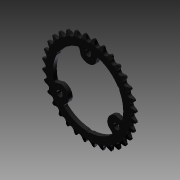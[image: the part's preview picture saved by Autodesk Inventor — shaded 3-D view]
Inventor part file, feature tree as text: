
AUTODESK INVENTOR PART (.ipt)
format: ipt  version: 2012 (Build 160160000, 160)  size: 849,408 bytes
history: native  units: in
note: dims shown in document units (in); Inventor stores cm internally (conversion verified against a paired STEP export)
features: boolean_combine x1, extrude x1, imported_body x1, sketch x1
ambient origin geometry x8: Origin, YZ Plane, XZ Plane, XY Plane, X Axis, Y Axis, Z Axis, Center Point
feature tree (4):
  boolean_combine  "Combine1"
  extrude  "Extrusion1"  [1 undecoded]
  imported_body  "Base1"
  sketch  "Sketch1"  dims[d0=1.0in d1=0.0in]
note: 1 required parameter value undecoded (feature->parameter linkage not recoverable at this tier; creation-order binding heuristic only, values carry confidence <= 0.55)
